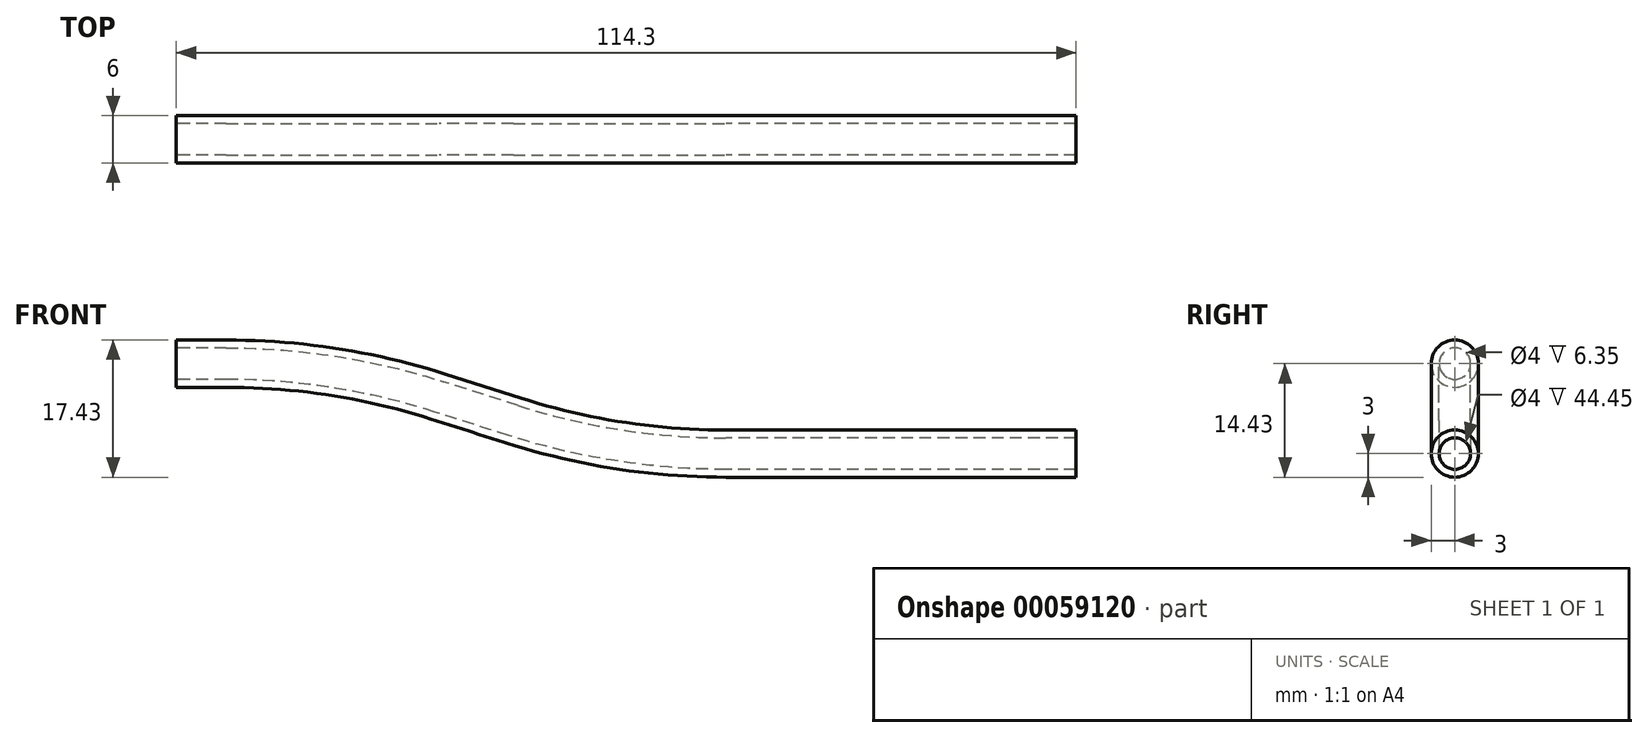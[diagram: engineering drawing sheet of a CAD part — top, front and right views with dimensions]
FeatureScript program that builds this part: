
annotation { "Feature Type Name" : "Feature", "Feature Type Description" : "" }
export const myFeature = defineFeature(function(context is Context, id is Id, definition is map)
    precondition{}
    {
        {
            var Q0;
            Q0=qCreatedBy(makeId("Right.planeOp"),FACE);
            var sketch = newSketch(context, id + "F0", { "sketchPlane" : qUnion([Q0])});
            skCircle(sketch, "E0", {"center": v(0, 0) * mm, "radius": 2 * mm});
            skCircle(sketch, "E1", {"center": v(0, 0) * mm, "radius": 3 * mm});
            skSolve(sketch);
        }
        {
            var Q0;
            Q0=qCreatedBy(makeId("Front.planeOp"),FACE);
            var sketch = newSketch(context, id + "F1", { "sketchPlane" : qUnion([Q0])});
            skLineSegment(sketch, "E2", {"start": v(0, 0) * mm, "end": v(-44.45, 0) * mm});
            skLineSegment(sketch, "E3", {"start": v(-71.48, 4.2) * mm, "end": v(-80.92, 7.22) * mm});
            skLineSegment(sketch, "E4", {"start": v(-107.95, 11.43) * mm, "end": v(-114.3, 11.43) * mm});
            skPoint(sketch, "E5.visualSharp", {"position": v(-94.1, 11.43) * mm});
            skArc(sketch, "E5.filletArc", {"start": v(-80.92, 7.22) * mm, "mid": v(-94.27, 10.37) * mm, "end": v(-107.95, 11.43) * mm});
            skPoint(sketch, "E6.visualSharp", {"position": v(-58.3, 0) * mm});
            skArc(sketch, "E6.filletArc", {"start": v(-71.48, 4.2) * mm, "mid": v(-58.13, 1.06) * mm, "end": v(-44.45, 0) * mm});
            skSolve(sketch);
        }
        {
            var Q0;
            Q0 = qSketchRegion(id + "F0", true);
            var Q1;
            Q1 = qConstructionFilter(qBodyType(qCreatedBy(id + "F1" ,EDGE), BodyType.WIRE), ConstructionObject.NO);
            sweep(context, id + "F2", {"profiles" : qUnion([Q0]), "path" : qUnion([Q1])});
        }
    });
